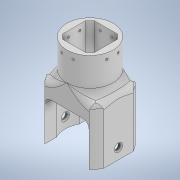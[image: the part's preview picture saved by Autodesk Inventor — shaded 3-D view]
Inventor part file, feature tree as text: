
AUTODESK INVENTOR PART (.ipt)
format: ipt  version: 2021 (Build 250183000, 183)  size: 500,736 bytes
history: native  units: mm
features: extrude x12, sketch x12, fillet x10, other x1
ambient origin geometry x8: Origin, YZ Plane, XZ Plane, XY Plane, X Axis, Y Axis, Z Axis, Center Point
bodies: Body1 (feature_tree)
feature tree (35):
  other  "Sólido1"
  extrude  "Extrusión1"  Depth=8.0mm
  extrude  "Extrusión2"  Depth=2.0mm
  fillet  "Empalme1"  Radius=400.0mm
  extrude  "Extrusión3"  Depth=40.0mm TaperAngle=0.0deg
  extrude  "Extrusión4"  Depth=12.0mm TaperAngle=0.0deg
  extrude  "Extrusión5"  Depth=160.0mm TaperAngle=0.0deg
  extrude  "Extrusión7"  Depth=2.0mm
  extrude  "Extrusión8"  Depth=50.0mm TaperAngle=0.0deg
  extrude  "Extrusión9"  Depth=10.0mm
  fillet  "Empalme2"  Radius=10.0mm
  fillet  "Empalme3"  Radius=10.0mm
  extrude  "Extrusión10"  Depth=10.0mm
  extrude  "Extrusión11"  Depth=10.0mm
  fillet  "Empalme4"  Radius=3.0mm
  fillet  "Empalme5"  Radius=500.0mm
  fillet  "Empalme6"  Radius=3.0mm
  fillet  "Empalme7"  Radius=3.0mm
  fillet  "Empalme8"  Radius=500.0mm
  fillet  "Empalme9"  [1 undecoded]
  fillet  "Empalme10"  [1 undecoded]
  extrude  "Extrusión12"  [1 undecoded]
  extrude  "Extrusión13"  [1 undecoded]
  sketch  "Boceto1"  dims[d7=40.0mm d8=0.0mm d10=8.0mm]
  sketch  "Boceto2"  dims[d11=400.0mm d12=0.0mm d13=2.0mm d16=400.0mm d17=0.0mm]
  sketch  "Boceto3"  dims[d18=400.0mm d19=0.0mm d20=40.0mm d21=0.0mm]
  sketch  "Boceto4"  dims[d25=62.249mm d26=0.0mm d27=12.0mm d28=0.0mm]
  sketch  "Boceto5"  dims[d32=9.0mm d37=160.0mm d38=0.0mm]
  sketch  "Boceto8"  dims[d39=2.0mm d40=2.0mm]
  sketch  "Boceto9"  dims[d47=160.0mm d48=0.0mm d49=50.0mm d50=0.0mm]
  sketch  "Boceto13"  dims[d51=10.0mm d52=10.0mm d53=10.0mm d54=10.0mm]
  sketch  "Boceto15"  dims[d55=10.0mm d56=10.0mm]
  sketch  "Boceto16"  dims[d57=10.0mm d62=3.0mm d63=3.0mm d64=500.0mm d65=0.0mm d70=3.0mm d71=3.0mm d72=500.0mm d73=0.0mm]
  sketch  "Boceto17"
  sketch  "Boceto18"
note: 4 required parameter values undecoded (feature->parameter linkage not recoverable at this tier; creation-order binding heuristic only, values carry confidence <= 0.55)
